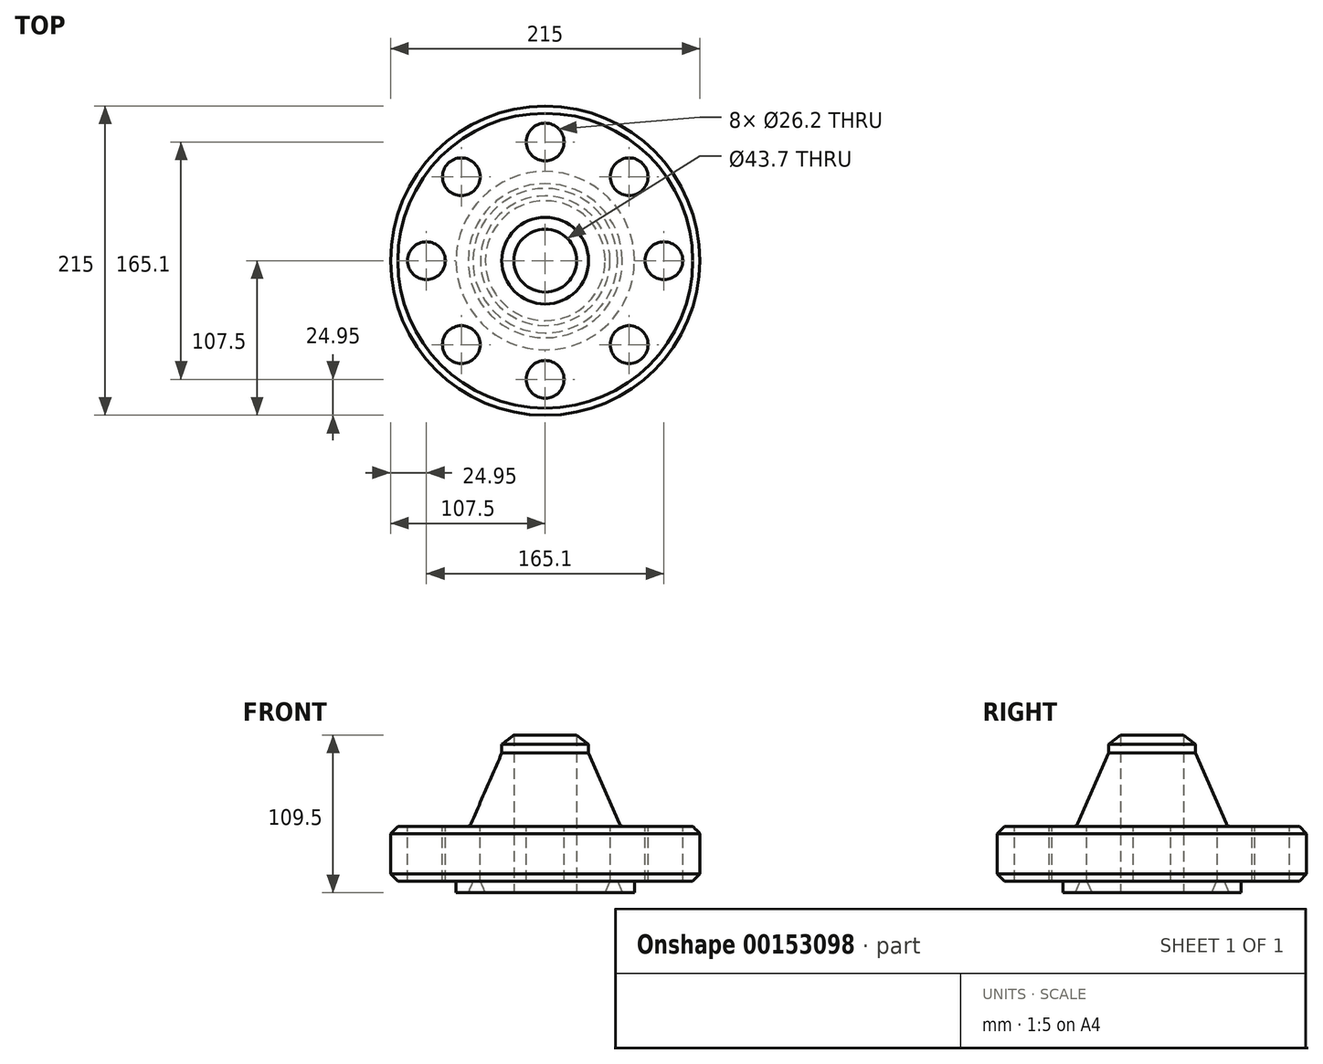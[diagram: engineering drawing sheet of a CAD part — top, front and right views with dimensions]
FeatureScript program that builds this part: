
annotation { "Feature Type Name" : "Feature", "Feature Type Description" : "" }
export const myFeature = defineFeature(function(context is Context, id is Id, definition is map)
    precondition{}
    {
        {
            var Q0;
            Q0=qCreatedBy(makeId("Front.planeOp"),FACE);
            var sketch = newSketch(context, id + "F0", { "sketchPlane" : qUnion([Q0])});
            skLineSegment(sketch, "E0", {"start": v(21.85, 0) * mm, "end": v(41.67, 0) * mm});
            skLineSegment(sketch, "E1", {"start": v(62, 0) * mm, "end": v(62, 8) * mm});
            skLineSegment(sketch, "E2", {"start": v(62, 8) * mm, "end": v(107.5, 8) * mm});
            skLineSegment(sketch, "E3", {"start": v(107.5, 8) * mm, "end": v(107.5, 46.1) * mm});
            skLineSegment(sketch, "E4", {"start": v(107.5, 46.1) * mm, "end": v(52.4, 46.1) * mm});
            skLineSegment(sketch, "E5", {"start": v(21.85, 0) * mm, "end": v(21.85, 109.5) * mm});
            skLineSegment(sketch, "E6", {"start": v(21.85, 109.5) * mm, "end": v(30.15, 103.13) * mm});
            skLineSegment(sketch, "E7", {"start": v(30.15, 103.13) * mm, "end": v(30.15, 97.13) * mm});
            skLineSegment(sketch, "E8", {"start": v(30.15, 97.13) * mm, "end": v(52.4, 46.1) * mm});
            skLineSegment(sketch, "E9", {"start": v(0, 0) * mm, "end": v(0, 157.84) * mm, "construction": true});
            skLineSegment(sketch, "E10", {"start": v(41.67, 0) * mm, "end": v(45.04, 7.94) * mm});
            skLineSegment(sketch, "E11", {"start": v(45.04, 7.94) * mm, "end": v(50.2, 7.94) * mm});
            skLineSegment(sketch, "E12", {"start": v(50.2, 7.94) * mm, "end": v(53.58, 0) * mm});
            skLineSegment(sketch, "E13.trimOffspring", {"start": v(53.58, 0) * mm, "end": v(62, 0) * mm});
            skSolve(sketch);
        }
        {
            var Q0;
            Q0=makeQuery(id+"F0.imprint","IMPRINT",FACE,{"disambiguationData":[TD([[makeQuery(id+"F0.imprint","IMPRINT",EDGE,{"derivedFrom":sQuery(id+"F0.wireOp",EDGE,"E0")}),1.0]])]});
            var Q1;
            Q1=sQuery(id+"F0.wireOp",EDGE,"E9");
            revolve(context, id + "F1", {"entities" : qUnion([Q0]), "axis" : qUnion([Q1]), "revolveType" : RevolveType.FULL});
        }
        {
            var Q0;
            Q0=makeQuery(id+"F1.opRevolve","SWEPT_FACE",FACE,{"disambiguationData":[OSD([sQuery(id+"F0.wireOp",EDGE,"E4")])]});
            var sketch = newSketch(context, id + "F2", { "sketchPlane" : qUnion([Q0])});
            skLineSegment(sketch, "E14", {"start": v(0, 0) * mm, "end": v(82.55, 0) * mm, "construction": true});
            skPoint(sketch, "E15", {"position": v(82.55, 0) * mm});
            skPoint(sketch, "E16.1.0", {"position": v(58.37, 58.37) * mm});
            skPoint(sketch, "E16.2.0", {"position": v(0, 82.55) * mm});
            skPoint(sketch, "E16.3.0", {"position": v(-58.37, 58.37) * mm});
            skPoint(sketch, "E16.4.0", {"position": v(-82.55, 0) * mm});
            skPoint(sketch, "E16.5.0", {"position": v(-58.37, -58.37) * mm});
            skPoint(sketch, "E16.6.0", {"position": v(0, -82.55) * mm});
            skPoint(sketch, "E16.7.0", {"position": v(58.37, -58.37) * mm});
            skPoint(sketch, "E16.center", {"position": v(0, 0) * mm});
            skSolve(sketch);
        }
        {
            var Q0;
            Q0=sQuery(id+"F2.wireOp",VERTEX,"E16.2.0");
            var Q1;
            Q1=sQuery(id+"F2.wireOp",VERTEX,"E16.1.0");
            var Q2;
            Q2=sQuery(id+"F2.wireOp",VERTEX,"E15");
            var Q3;
            Q3=sQuery(id+"F2.wireOp",VERTEX,"E16.7.0");
            var Q4;
            Q4=sQuery(id+"F2.wireOp",VERTEX,"E16.6.0");
            var Q5;
            Q5=sQuery(id+"F2.wireOp",VERTEX,"E16.5.0");
            var Q6;
            Q6=sQuery(id+"F2.wireOp",VERTEX,"E16.4.0");
            var Q7;
            Q7=sQuery(id+"F2.wireOp",VERTEX,"E16.3.0");
            var Q8;
            Q8=makeQuery(id+"F1.opRevolve","SWEPT_BODY",BODY,{"disambiguationData":[OSD([sQuery(id+"F0.wireOp",EDGE,"E0"),sQuery(id+"F0.wireOp",EDGE,"E1"),sQuery(id+"F0.wireOp",EDGE,"E2"),sQuery(id+"F0.wireOp",EDGE,"E3"),sQuery(id+"F0.wireOp",EDGE,"E4"),sQuery(id+"F0.wireOp",EDGE,"E5"),sQuery(id+"F0.wireOp",EDGE,"E6"),sQuery(id+"F0.wireOp",EDGE,"E7"),sQuery(id+"F0.wireOp",EDGE,"E8"),sQuery(id+"F0.wireOp",EDGE,"E10"),sQuery(id+"F0.wireOp",EDGE,"E11"),sQuery(id+"F0.wireOp",EDGE,"E12"),sQuery(id+"F0.wireOp",EDGE,"E13.trimOffspring")])]});
            hole(context, id + "F3", {"style" : HoleStyle.SIMPLE, "endStyle" : HoleEndStyle.THROUGH, "standardTappedOrClearance" : lookupTablePath({ "standard" : "ANSI", "fit" : "Normal (ASME)", "size" : "1", "type" : "Clearance" }), "standardBlindInLast" : lookupTablePath({ "fit" : "Free", "standard" : "ANSI", "size" : "1", "type" : "Clearance" }), "holeDiameter" : 26.2 * mm, "locations" : qUnion([Q0, Q1, Q2, Q3, Q4, Q5, Q6, Q7]), "scope" : qUnion([Q8]), "isTappedThrough" : true});
        }
        {
            var Q0;
            Q0=makeQuery(id+"F1.opRevolve","SWEPT_EDGE",EDGE,{"disambiguationData":[OSD([sQuery(id+"F0.wireOp",EDGE,"E4"),sQuery(id+"F0.wireOp",EDGE,"E8")])]});
            fillet(context, id + "F4", {"entities" : qUnion([Q0]), "radius" : 3 * mm, "tangentPropagation" : true, "allowEdgeOverflow" : false});
        }
        {
            var Q0;
            Q0=makeQuery(id+"F1.opRevolve","SWEPT_EDGE",EDGE,{"disambiguationData":[OSD([sQuery(id+"F0.wireOp",EDGE,"E2"),sQuery(id+"F0.wireOp",EDGE,"E3")])]});
            chamfer(context, id + "F5", {"entities" : qUnion([Q0]), "width" : 5 * mm, "tangentPropagation" : true});
        }
        {
            var Q0;
            Q0=makeQuery(id+"F1.opRevolve","SWEPT_EDGE",EDGE,{"disambiguationData":[OSD([sQuery(id+"F0.wireOp",EDGE,"E3"),sQuery(id+"F0.wireOp",EDGE,"E4")])]});
            chamfer(context, id + "F6", {"entities" : qUnion([Q0]), "width" : 5 * mm, "tangentPropagation" : true});
        }
    });
